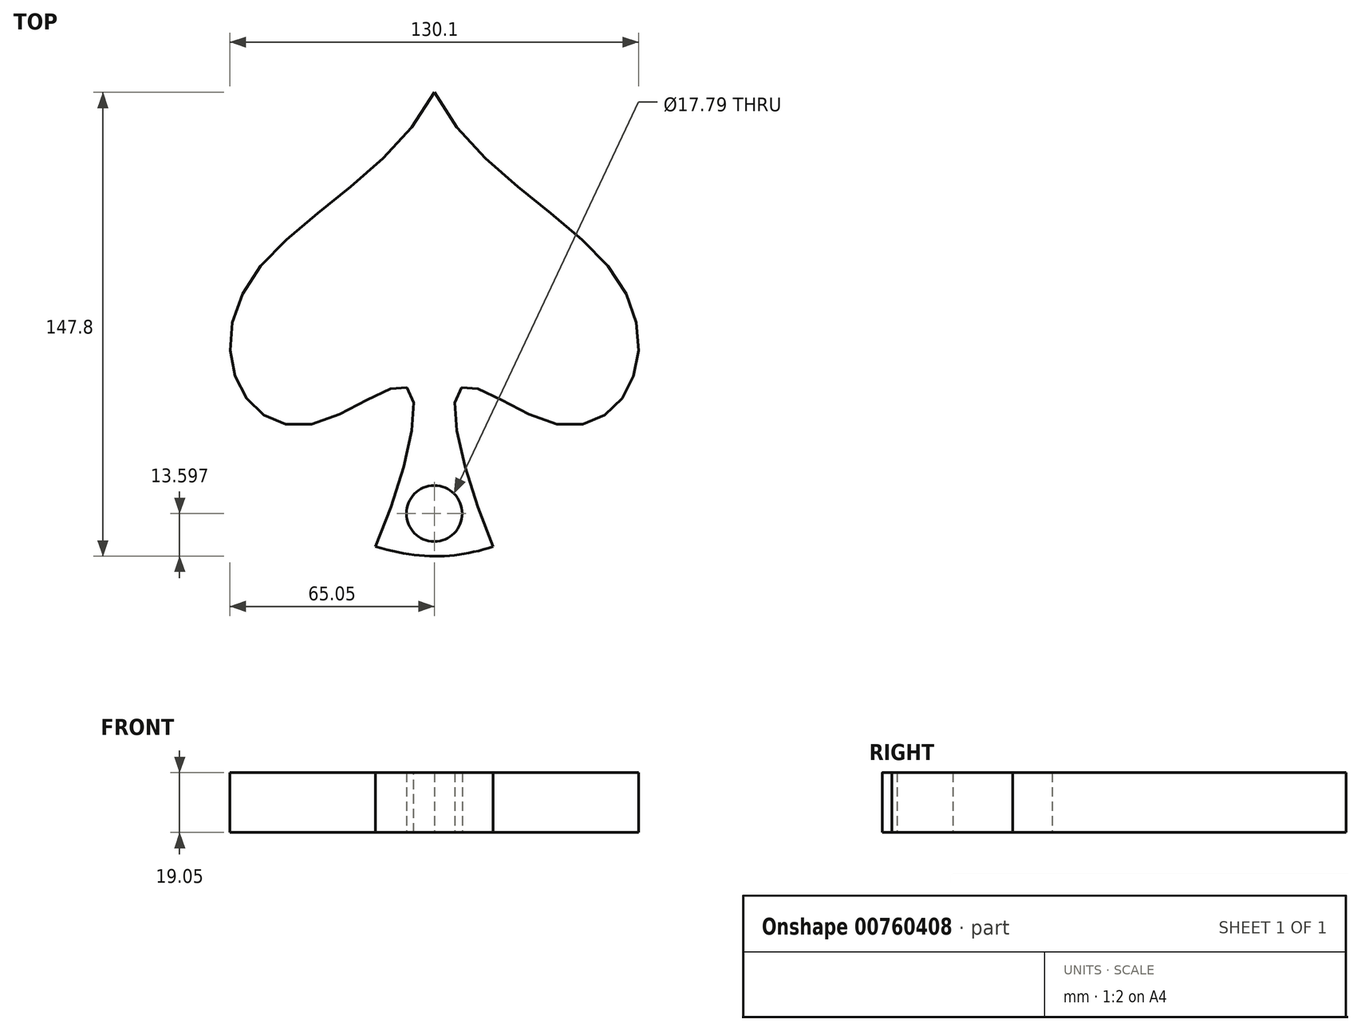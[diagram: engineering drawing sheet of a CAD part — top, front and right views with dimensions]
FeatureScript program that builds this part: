
annotation { "Feature Type Name" : "Feature", "Feature Type Description" : "" }
export const myFeature = defineFeature(function(context is Context, id is Id, definition is map)
    precondition{}
    {
        {
            var Q0;
            Q0=qCreatedBy(makeId("Top.planeOp"),FACE);
            var sketch = newSketch(context, id + "F0", { "sketchPlane" : qUnion([Q0])});
            skFitSpline(sketch, "E0", {"points": [v(18.7, -50.63) * mm, v(8.74, 0) * mm, v(38.7, -11.61) * mm, v(61.9, 0) * mm, v(57.2, 36.26) * mm, v(0, 94.12) * mm], "startDerivative": vector(-115.95, 273.66) * mm, "endDerivative": vector(-133.9, 272.5) * mm});
            skLineSegment(sketch, "E1", {"start": v(0, -30.78) * mm, "end": v(0, 38.6) * mm, "construction": true});
            skFitSpline(sketch, "E2.MirrorCS", {"points": [v(-18.7, -50.63) * mm, v(-8.74, 0) * mm, v(-38.7, -11.61) * mm, v(-61.9, 0) * mm, v(-57.2, 36.26) * mm, v(0, 94.12) * mm], "startDerivative": vector(115.95, 273.66) * mm, "endDerivative": vector(133.9, 272.5) * mm});
            skFitSpline(sketch, "E3", {"points": [v(-18.7, -50.63) * mm, v(18.7, -50.63) * mm], "startDerivative": vector(42.46, -12.73) * mm, "endDerivative": vector(35.3, 11.65) * mm});
            skCircle(sketch, "E4", {"center": v(0, -40.08) * mm, "radius": 8.9 * mm});
            skSolve(sketch);
        }
        {
            var Q0;
            Q0=makeQuery(id+"F0.imprint","IMPRINT",FACE,{"disambiguationData":[TD([[makeQuery(id+"F0.imprint","IMPRINT",EDGE,{"derivedFrom":sQuery(id+"F0.wireOp",EDGE,"E0")}),1.0]])]});
            extrude(context, id + "F1", {"entities" : qUnion([Q0]), "depth" : 19.05 * mm, "offsetDistance" : 25.4 * mm});
        }
    });
